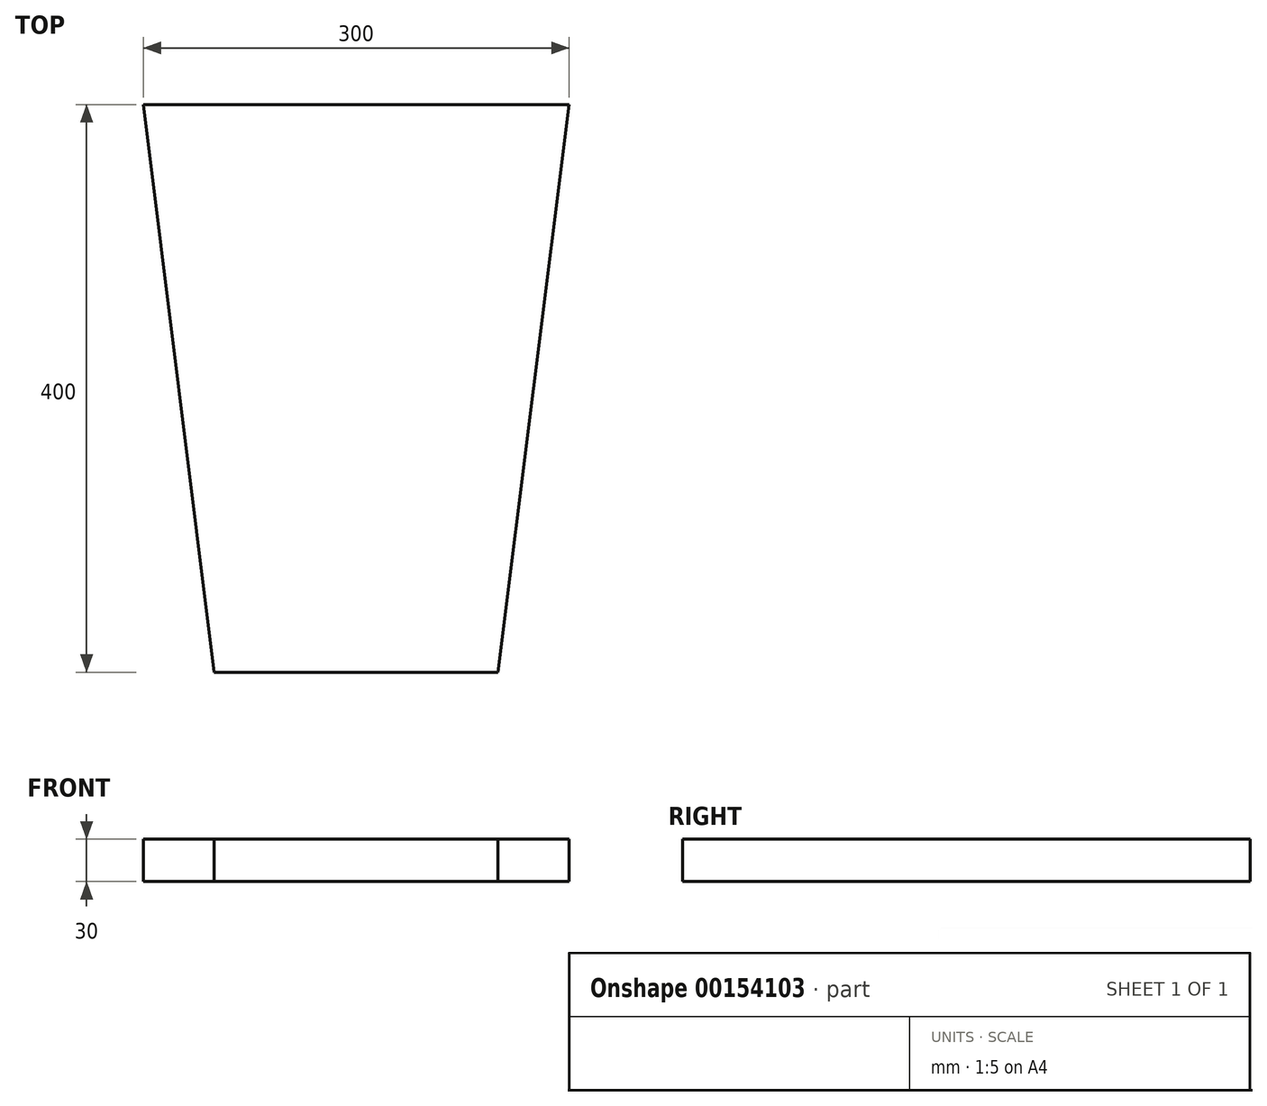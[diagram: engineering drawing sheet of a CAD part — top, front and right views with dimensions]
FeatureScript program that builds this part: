
annotation { "Feature Type Name" : "Feature", "Feature Type Description" : "" }
export const myFeature = defineFeature(function(context is Context, id is Id, definition is map)
    precondition{}
    {
        {
            var Q0;
            Q0=qCreatedBy(makeId("Top.planeOp"),FACE);
            var sketch = newSketch(context, id + "F0", { "sketchPlane" : qUnion([Q0])});
            skLineSegment(sketch, "E0", {"start": v(0, 0) * mm, "end": v(0, 200) * mm});
            skLineSegment(sketch, "E1", {"start": v(0, 200) * mm, "end": v(150, 200) * mm});
            skLineSegment(sketch, "E2", {"start": v(0, 0) * mm, "end": v(0, -200) * mm});
            skLineSegment(sketch, "E3", {"start": v(0, -200) * mm, "end": v(100, -200) * mm});
            skLineSegment(sketch, "E4", {"start": v(100, -200) * mm, "end": v(150, 200) * mm});
            skLineSegment(sketch, "E5.MirrorCS", {"start": v(0, 200) * mm, "end": v(-150, 200) * mm});
            skLineSegment(sketch, "E6.MirrorCS", {"start": v(-100, -200) * mm, "end": v(-150, 200) * mm});
            skLineSegment(sketch, "E7.MirrorCS", {"start": v(0, -200) * mm, "end": v(-100, -200) * mm});
            skSolve(sketch);
        }
        {
            var Q0;
            Q0 = qSketchRegion(id + "F0", true);
            extrude(context, id + "F1", {"entities" : qUnion([Q0]), "depth" : 30 * mm});
        }
    });
